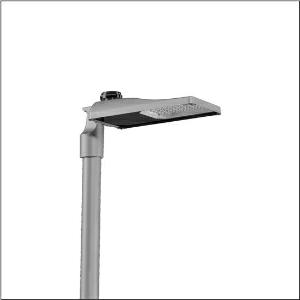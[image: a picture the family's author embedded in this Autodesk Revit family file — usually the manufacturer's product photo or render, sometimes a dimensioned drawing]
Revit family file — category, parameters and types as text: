
# Revit family: streetlight_sl_31_mini___st1_0a_5xh2d3bn08ha_f2e6
name_source: partatom
category: Lighting Fixtures
units: mm (PartAtom-declared; Revit-internal decimal feet)

## family parameters
Cut with Voids When Loaded = No
Host = Face
Light Source = No
Part Type = Normal
Room Calculation Point = No
Round Connector Dimension = Use Diameter
Shared = No

## types (1)
- --- (1 x LED, 9240 lm, 68.3 W, 3000K)
    Apparent Load = 68 VA
    CIE Flux Codes = 37 72 97 100 100
    Color Rendering = 70
    Color Temperature = 3000K
    Default Elevation = 1800 mm
    Description = Streetlight SL 31 mini, mast luminaire, primary light control with lens, of PMMA, primary optical cover: cover, of toughened safety glass, transparent, light distribution: ST1.0a, light emission: direct distribution, primary light characteristic: asymmetric, installation type: post-top, side-entry, LED, High Power LED, rated luminous flux: 9.240lm, luminous efficacy: 135lm/W, light colour: 730, colour temperature: 3000K, control: overheat protection, intelligent temperature release in ECG and LED module, constant luminous flux control, time-dependent luminous flux control, flexible luminous flux parameterisation, presetting dimming linear, with cable H07RN-F 3x 1.5mm², mains connection: 220..240V, AC, 50/60Hz, connection cable pre-assembled, cable length: 8,5m, start of lifetime: 68W, end of service life: 75W, reduction: 30W, luminaire housing, of diecast aluminium, powder-coated, Siteco® metallic grey (DB 702S), corrosivity category C5 high according to DIN EN ISO 12944, no sealing on luminaire upper side, inclination: -15°..+20° (post-top) | -20°..+20° (side-entry), adjustable in 5° steps, mast flange (76/60mm) included as standard, multi-level sealing system, sealing non-destructively replaceable, protection rating (complete): IP66, insulation class (complete): insulation class I (protective earthing), certification: CE, ENEC, ENEC+, VDE, UKCA, impact resistance: IK09, permissible operating ambient temperature for outdoor applications: -40..+50°C, standard-compliant lighting for roads and squares, packaging unit: 1 piece

Light Distribution: ST1.0a
    Height = 76 mm
    Lamp = 1 x LED
    Lamp Light Flux = 9240 lm
    Lamp Power = 68.3 W
    Lamp count = 1
    Length = 547 mm
    Luminous efficacy = 135 lm/W
    Manufacturer = Siteco
    ModVariant = No
    Model = 5XH2D3BN08HA
    Number of Poles = 1
    OnlyDefault = Yes
    Power Factor = 1
    Product Name = Streetlight SL 31 mini | ST1.0a
    Product group = mast luminaire | pylon top
    ProductGroupID = 6100
    Protection Class = Protection class I
    Protection Degree = IP 66
    RLX_Detail_Level = 1
    RLX_Emergency_Light_Flux = 0 lm
    RLX_Emergency_Type = 0
    RLX_Emergency_Type_DB = No
    RlxData = <blob elided: 40369 chars, md5=db27cb1c>
    Socket = socket
    Standby Power = 0 W
    System Light Flux = 9240 lm
    System Power = 68 W
    Type Comments = factory setting: luminous flux: 100 % | dim-lin: 254 | 693 mA
    Type Image = l_1300322.jpg
    URL = http://relux.com
    VarID = @adj_012573
    Voltage = 0 V
    Weight = 0.00 kg
    Width = 265 mm

## geometry (parser evidence)
native form markers: Blend x4, Sweep x10
no freeform markers — native parametric forms only
